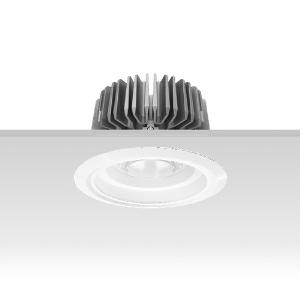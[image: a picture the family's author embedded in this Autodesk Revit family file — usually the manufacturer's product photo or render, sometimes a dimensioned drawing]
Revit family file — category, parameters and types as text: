
# Revit family: 3f_filippi_-_3f_reno_bianco_ampio_3f_filippi_-_30383_a01023_-_3f_reno_150_wh_3000-840_dali_wide___vt_wh_d9f4
name_source: partatom
category: Lighting Fixtures
units: mm (PartAtom-declared; Revit-internal decimal feet)

## family parameters
Cut with Voids When Loaded = No
Host = Face
Light Source = No
Part Type = Normal
Room Calculation Point = No
Round Connector Dimension = Use Diameter
Shared = No

## types (1)
- 3F Filippi - 3F Reno Bianco Ampio (1 x LED, 2647 lm, 28 W, 4000 K)
    Apparent Load = 28 VA
    Approval mark = CE
    CIE Flux Codes = 74 93 99 100 100
    Color Rendering = 80
    Color Temperature = 4000 K
    Control Gear = Electronic transformer
    Default Elevation = 1800 mm
    Description = ILLUMINOTECHNICAL
Luminous efficiency 100% (DLOR 100%, ULOR 0%).
Initial luminous flux of the luminaire 2647 lm.
Direct symmetric wide distribution.
Installation Interdistance Transv.D = 1.54 x hu - Long.D = 1.54 x hu.
Tabular UGR (CIE 117 - 4H-8H; S=0.25H; 70/50/20): RUG 24.4 - 24.2.
Beam angle: 74° - 73°.
Luminous efficacy 95 lm/W.
Lifetime (L90/B10): 30000 h. (tq+25°C)
Lifetime (L85/B10): 50000 h. (tq+25°C)
Lifetime (L70/B10): 80000 h. (tq+25°C)
Sudden decreased luminous flux after 50000 hours: 0% (C0).
Photobiological safety in compliance with IEC/TR 62778: RG0 risk exempt, (IEC 62471).
In compliance with IEC/EN 62722-2-1 - IEC/EN 62717 standards.

SOURCE
Compact LED module 3000/840.
Energy efficiency class (UE 2019/2020 - UE 2019/2015): E.
CIE 13.3 Colour rendering index: CRI >80 (R9 <50%).
IES TM-30 Fidelity Index: Rf = 84 Rg = 95.
CCT nominal colour temperature 4000 K.
Colour initial tolerance (MacAdam): SDCM 3.
Zhaga Book 3 compliant.

MECHANICAL
Passive heat dissipator in die-casting aluminium, oversized, for optimum thermal management of the LED module.
Parabolic element with graduated/concentric rings in white polycarbonate.
Transparent external lens with glossy and satin differentiated surfaces, with a cooling and anti-insect system in methacrylate (PMMA).
Fastening spring clips in stainless steel.
Dimensions: diameter 176 mm, height 111 mm. Weight 1.4 kg.
IP44 protection degree for exposed part, IP20 for recessed part.
Mechanical strength to impacts IK06 (1 joule).
Glow-wire test resistance 650°C.

ELECTRICAL
Wiring on a separate unit.
Halogen Free DALI-2 DATI (Parts 251, 252, 253), PUSH-DIM, electronic wiring 230V-50/60Hz, power factor 0.97 at full load, THD <25%, constant output current, SELV, class II, 1 driver, 1 DALI addresse.
Power of the luminaire 28 W.
ENEC - CE.
SAFE FLICKER: PstLM=<1 and SVM=<0.4 (IEC TR 61547-1 and IEC TR 63158), to ensure a more comfortable and safe light.
Luminaire compliant with EN 60598-2-22 for power supply from a centralised emergency system CPSS (Central Power Supply System), not incorporated in the luminaire - high risk areas excluded. The default power and flux are 100% in AC and 100% in DC.
Ambient temperature from 0°C to +25°C.
Temperature class T6 max 85°C.
Relative humidity UR: <85%.

INSTALLATION
Pull-up recessed fitting.
False ceiling carving: 150 mm.
All accessories dedicated to this product are available on the Catalog and on our website www.3F-Filippi.com.

ACCESSORIES
A01023 - VT transparent glass, tempered, not flammable, locked and in line with the trim, in white polycarbonate.

APPLICATIONS
Environments: architectural, commercial, exhibition areas, transit areas, corridors, shops, display windows, service areas.
In false ceilings with narrow voids.

LIGHT MANAGEMENT
Recommended minimum setting: 10%.
The luminaire, equipped with (DALI-2 DATI) driver, can be controlled manually with 3F Easy Dim technology or automatically/manually with wired or wireless DALI/D2D control systems.
The D2D driver guarantees interoperability with other devices with the same certification by making the following information available:
Device Data (Part 251), Energy Report (Part 252), Diagnosis & Maintenance (Part 253).
In electrical systems without a regulation system (manual or automatic) and DALI bus, a suitable jumper must be made on the DA-DA terminals of the appliance.

WARNING
Luminaire designed for disposal/recycling at end-of-life.
Replaceable (LED only) light source by a professional. Replaceable control gear by a professional.
    Height = 0 mm  [stored 0 ft]
    Lamp = 1 x LED
    Lamp Light Flux = 2647 lm
    Lamp Power = 28 W
    Lamp count = 1
    Length = 176 mm
    Lifetime = 50000 h
    Luminous efficacy = 95 lm/W
    Manufacturer = 3F Filippi
    ModVariant = No
    Model = 3F Filippi - 30383+A01023 - 3F Reno 150 WH 3000-840 DALI WIDE + VT WH
    Mounting Place = Ceiling
    Mounting Type = Recessed
    Number of Poles = 1
    OnlyDefault = Yes
    Power Factor = 1
    Product Name = 3F Filippi - 3F Reno Bianco Ampio
    Product group = recessed luminaire
    ProductGroupID = 4
    Protection Class = Protection class II
    Protection Degree = IP 20
    RLX_Detail_Level = 1
    RLX_Emergency_Light_Flux = 0 lm
    RLX_Emergency_Type = 0
    RLX_Emergency_Type_DB = No
    RlxData = <blob elided: 87857 chars, md5=836f1e03>
    Socket = socket
    Standby Power = 0 W
    System Light Flux = 2647 lm
    System Power = 28 W
    Type Comments = Product without accessories
    Type Image = 3ffilippi_3f_reno_150_wh_d150__a01023.jpg
    URL = http://relux.com
    VarID = ---
    Voltage = 0 V
    Weight = 0.00 kg
    Width = 0 mm  [stored 0 ft]

note: [stored X ft] marks values corroborated as IEEE doubles in the binary element streams (Revit-internal decimal feet)

## geometry (parser evidence)
native form markers: Blend x4, Sweep x10
no freeform markers — native parametric forms only
